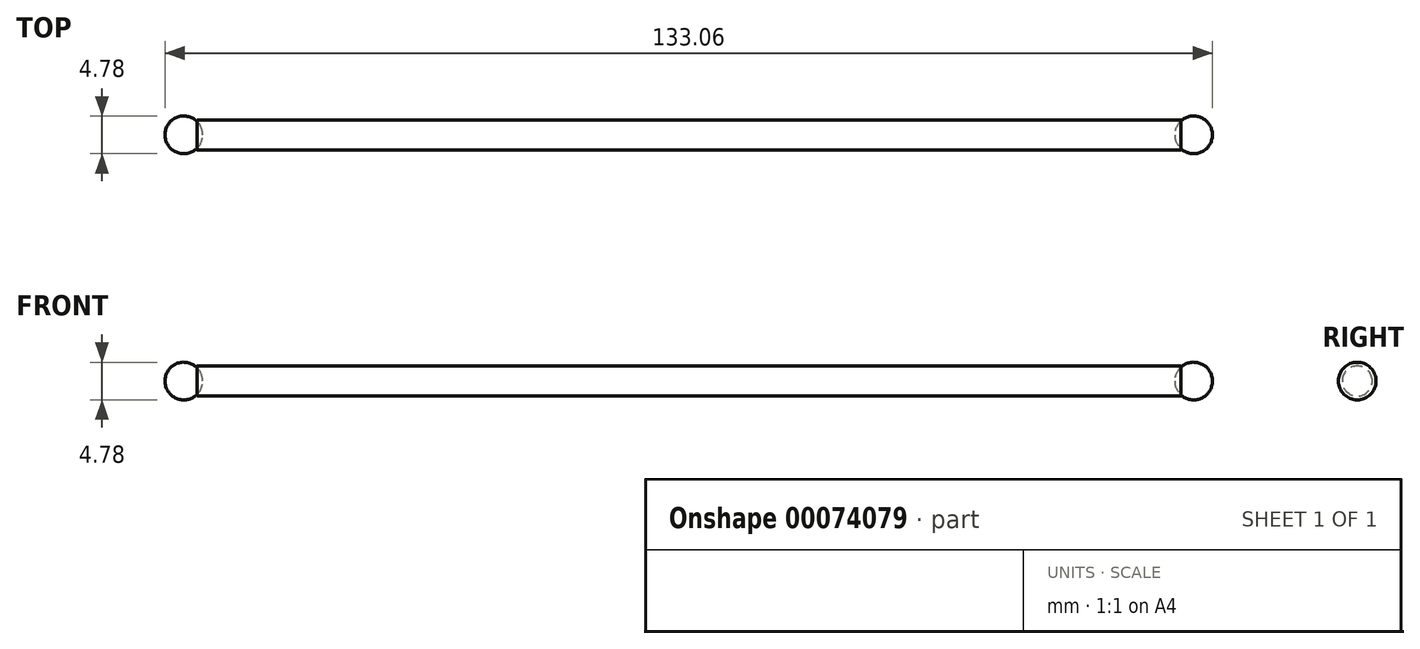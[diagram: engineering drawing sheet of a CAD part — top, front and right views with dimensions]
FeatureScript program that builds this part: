
annotation { "Feature Type Name" : "Feature", "Feature Type Description" : "" }
export const myFeature = defineFeature(function(context is Context, id is Id, definition is map)
    precondition{}
    {
        {
            var Q0;
            Q0=qCreatedBy(makeId("Right.planeOp"),FACE);
            var sketch = newSketch(context, id + "F0", { "sketchPlane" : qUnion([Q0])});
            skCircle(sketch, "E0", {"center": v(0, 0) * mm, "radius": 1.91 * mm});
            skSolve(sketch);
        }
        {
            var Q0;
            Q0 = qSketchRegion(id + "F0", true);
            extrude(context, id + "F1", {"entities" : qUnion([Q0]), "endBound" : BoundingType.SYMMETRIC, "depth" : 124.97 * mm});
        }
        {
            var Q0;
            Q0=qCreatedBy(makeId("Top.planeOp"),FACE);
            var sketch = newSketch(context, id + "F2", { "sketchPlane" : qUnion([Q0])});
            skArc(sketch, "E1", {"start": v(66.5, 0) * mm, "mid": v(64.12, 2.4) * mm, "end": v(61.72, 0) * mm});
            skLineSegment(sketch, "E2", {"start": v(61.72, 0) * mm, "end": v(66.5, 0) * mm});
            skSolve(sketch);
        }
        {
            var Q0;
            Q0 = qSketchRegion(id + "F2", true);
            var Q1;
            Q1=makeQuery(id+"F1.opExtrude","CAP_EDGE",EDGE,{"disambiguationData":[OSD([sQuery(id+"F0.wireOp",EDGE,"E0")])],"isStart":false});
            revolve(context, id + "F3", {"entities" : qUnion([Q0]), "axis" : qUnion([Q1]), "revolveType" : RevolveType.FULL});
        }
        {
            var Q0;
            Q0=makeQuery(id+"F3.opRevolve","SWEPT_BODY",BODY,{"disambiguationData":[OSD([sQuery(id+"F2.wireOp",EDGE,"E1"),sQuery(id+"F2.wireOp",EDGE,"E2")])]});
            var Q1;
            Q1=qCreatedBy(makeId("Right.planeOp"),FACE);
            transform(context, id + "F4", {"entities" : qUnion([Q0]), "transformType" : TransformType.TRANSLATION_DISTANCE, "transformDirection" : qUnion([Q1]), "distance" : 128.27 * mm, "oppositeDirection" : true, "makeCopy" : true});
        }
    });
